# Revit family: DC_Holyoake_OutsideLouver_OHCL-F-102_supply_13
name_source: partatom
category: Air Terminals
revit_build: Autodesk Revit 2014 (Build: 20130308_1515(x64)
units: mm (PartAtom-declared; Revit-internal decimal feet)

## types (2) — shared parameters
Accessories = Aluminium Bird mesh or insect mesh (fibreglass)
Blade Count = 7
Blade Cut Setout = 714 mm
Blade Height = 134.9 mm  [stored 0.442585 ft]
Blade Offset = 2.48 mm
Blade Pitch = 102 mm  [stored 0.334646 ft]
Blade Width = 101.4 mm  [stored 0.332677 ft]
Flange Width = 25.4 mm  [stored 0.0833333 ft]
Gang Bar Width (plus min. 300mm clearance) = 50 mm  [stored 0.164042 ft]
Gang Bar with Actuator Width (plus min. 300mm clearance) = 150 mm  [stored 0.492126 ft]
Louver Depth = 106.35 mm  [stored 0.348917 ft]
Manufacturer = Holyoake
Max Flow = 5000.0 L/s
Min Flow = 100.0 L/s
Overall Depth = 38.3 mm  [stored 0.125656 ft]
Static Pressure Max = 45.0 Pa
Static Pressure Min = 5.0 Pa

## per-type parameters (varying)
| type | Blade Array Count | Blade Control | Blade Length | Connector Height | Connector Width | Description | Exact Neck Height | Exact Neck Width | Exact Overall Flange Height | Exact Overall Flange Width | Holyoake Product Range | Material - Body | Material _ Face | Noise Level NC Max | Noise Level NC Min | Nominal Height | Nominal Width | Overall Opening | Top Blade Height | Type Comments | URL |
| OHL-F-102 | 7.970588 | No | 688 mm  [stored 2.25722 ft] | 789 mm | 664 mm | Holyoake Outside Horizontal Louvre | 860 mm | 735 mm  [stored 2.41142 ft] | 910.8 mm | 785.8 mm |  | <By Category> | <By Category> |  |  | 866 mm | 741 mm  [stored 2.4311 ft] | 813 mm | 99 mm | 102mm Horizontal Curved Profile Louvers in Flanged Surround | http://www.productspec.net |
| OHCL-F-102 | 7.578431 | Yes | 673 mm  [stored 2.20801 ft] | 749 mm  [stored 2.45735 ft] | 649 mm  [stored 2.12927 ft] | Closable Weather Louvres shall be Holyoake Model OHCL-F-102 curved profile 100mm louvred blades set at 102mm centres and constructed in a 107mm flanged (F) frame to suit the installation profile. Each Blade shall be fitted with a concealed damper blade pivoted on the underside of each fixed blade which is gang operated by either manual or motorised means. Closable Weather Louvres shall be of extruded aluminium construction and finished in natural anodised or powdercoat and fitted with accessories and dampers where indicated as manufactured by Holyoake. | 820 mm  [stored 2.69029 ft] | 720 mm  [stored 2.3622 ft] | 870.8 mm  [stored 2.85696 ft] | 770.8 mm  [stored 2.52887 ft] | Outside Louvres | Holyoake Aluminium | Holyoake Aluminium | 0.00 NC | 0.00 NC | 826 mm  [stored 2.70997 ft] | 726 mm  [stored 2.38189 ft] | 773 mm  [stored 2.53609 ft] | 59 mm | 102mm Closable Horizontal Curved Profile Louvers in Flanged Surround | http://www.holyoake.com |

note: column(s) folded — value = type name in every type: Model

note: [stored X ft] marks values corroborated as IEEE doubles in the binary element streams (Revit-internal decimal feet)

## geometry (parser evidence)
native form markers: Blend x4, Sweep x9
no freeform markers — native parametric forms only
